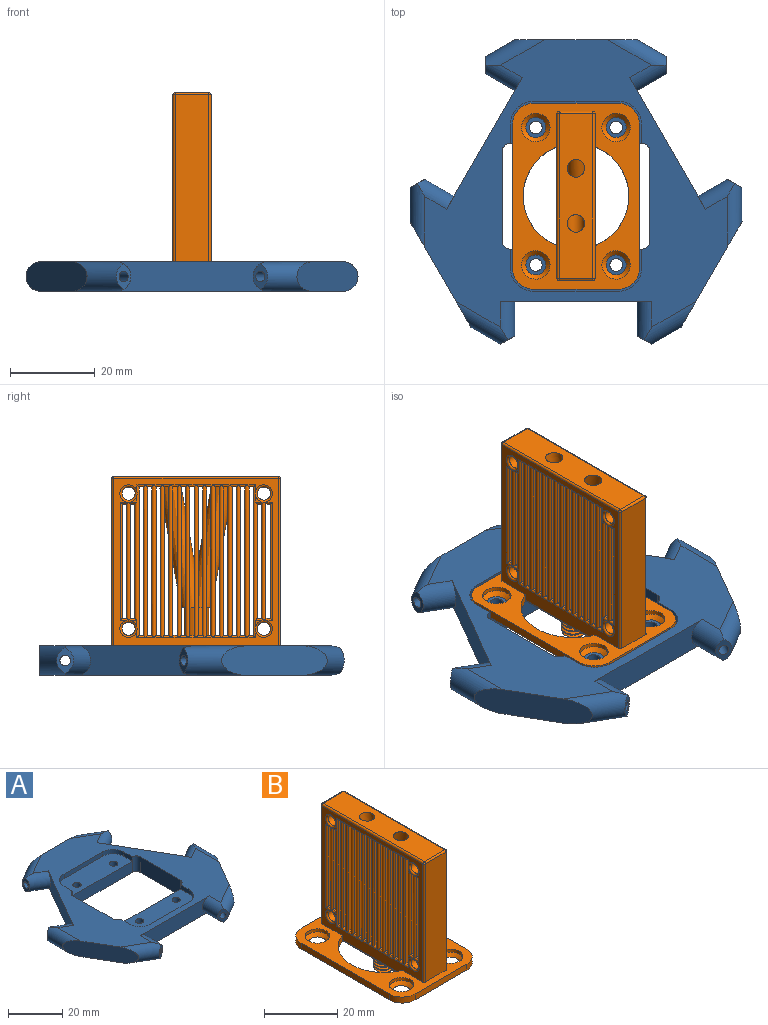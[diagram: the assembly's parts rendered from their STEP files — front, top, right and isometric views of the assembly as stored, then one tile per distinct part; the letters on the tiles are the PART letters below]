
ASSEMBLY  parts=2 mates=1
PART A: 53 faces, bbox 78.5x75.5x7 mm
  f0: plane 71.52x67.94mm, normal (0,0,1), area 1672.5mm2, adj f6,f8,f10,f12,f14,f16,f21,f22
  f1: cylinder r=1.5mm len=5mm, axis (0,0,1), area 47.1mm2, adj f5,f52
  f2: cylinder r=1.5mm len=5mm, axis (0,0,1), area 47.1mm2, adj f5,f52
  f3: cylinder r=1.5mm len=5mm, axis (0,0,1), area 47.1mm2, adj f5,f46
  f4: cylinder r=1.5mm len=5mm, axis (0,0,1), area 47.1mm2, adj f5,f46
  f5: plane 71.52x67.94mm, normal (0,0,-1), area 2238.2mm2, adj f1,f2,f3,f4,f6,f8,f10,f12
  f6: plane 31.06x17.93mm, normal (-0.87,0.5,0), area 212.6mm2, adj f0,f5,f21,f32
  f7: plane 6.04x3.46mm, normal (-0.5,0.87,0), area 12.2mm2, adj f20,f31,f32
  f8: plane 25x14.43mm, normal (-0.87,-0.5,0), area 181mm2, adj f0,f5,f30,f31
  f9: plane 6.04x3.46mm, normal (0.5,-0.87,0), area 12.2mm2, adj f20,f29,f30
  f10: plane 35.87x7mm, normal (0,-1,0), area 212.6mm2, adj f0,f5,f28,f29
  f11: plane 6.04x3.46mm, normal (-0.5,-0.87,0), area 12.2mm2, adj f19,f27,f28
  f12: plane 25x14.43mm, normal (0.87,-0.5,0), area 181mm2, adj f0,f5,f25,f27
  f13: plane 6.04x3.46mm, normal (0.5,0.87,0), area 12.2mm2, adj f19,f25,f26
  f14: plane 31.06x17.93mm, normal (0.87,0.5,0), area 212.6mm2, adj f0,f5,f24,f26
  f15: plane 6.04x4mm, normal (1,0,0), area 12.2mm2, adj f18,f23,f24
  f16: plane 28.87x7mm, normal (0,1,0), area 181mm2, adj f0,f5,f22,f23
  f17: plane 6.04x4mm, normal (-1,0,0), area 12.2mm2, adj f18,f21,f22
  f18: cylinder r=1.25mm len=42.72mm, axis (-1,0,0), area 335.6mm2, adj f15,f17
  f19: cylinder r=1.25mm len=38.25mm, axis (0.5,0.87,0), area 335.6mm2, adj f11,f13
  f20: cylinder r=1.25mm len=38.25mm, axis (0.5,-0.87,0), area 335.6mm2, adj f7,f9
  f21: cylinder r=3.5mm len=9.54mm, axis (-0.87,0.5,0), area 88.7mm2, adj f0,f5,f6,f17,f22
  f22: cylinder r=3.5mm len=14.79mm, axis (0.87,0.5,0), area 112.9mm2, adj f0,f5,f16,f17,f21
  f23: cylinder r=3.5mm len=14.79mm, axis (0.87,-0.5,0), area 112.9mm2, adj f0,f5,f15,f16,f24
  f24: cylinder r=3.5mm len=9.54mm, axis (-0.87,-0.5,0), area 88.7mm2, adj f0,f5,f14,f15,f23
  f25: cylinder r=3.5mm len=15.06mm, axis (0,-1,0), area 112.9mm2, adj f0,f5,f12,f13,f26
  f26: cylinder r=3.5mm len=9.54mm, axis (0.87,0.5,0), area 88.7mm2, adj f0,f5,f13,f14,f25
  f27: cylinder r=3.5mm len=14.79mm, axis (-0.87,-0.5,0), area 112.9mm2, adj f0,f5,f11,f12,f28
  f28: cylinder r=3.5mm len=9mm, axis (0,1,0), area 88.7mm2, adj f0,f5,f10,f11,f27
  f29: cylinder r=3.5mm len=9mm, axis (0,-1,0), area 88.7mm2, adj f0,f5,f9,f10,f30
  f30: cylinder r=3.5mm len=14.79mm, axis (-0.87,0.5,0), area 112.9mm2, adj f0,f5,f8,f9,f29
  f31: cylinder r=3.5mm len=15.06mm, axis (0,1,0), area 112.9mm2, adj f0,f5,f7,f8,f32
  f32: cylinder r=3.5mm len=9.54mm, axis (0.87,-0.5,0), area 88.7mm2, adj f0,f5,f6,f7,f31
  f33: plane 31x5mm, normal (0,1,0), area 155mm2, adj f5,f37,f39,f52
  f34: plane 21x7mm, normal (-1,0,0), area 147mm2, adj f0,f5,f39,f40
  f35: plane 31x5mm, normal (0,-1,0), area 155mm2, adj f5,f38,f40,f46
  f36: plane 21x7mm, normal (1,0,0), area 147mm2, adj f0,f5,f37,f38
  f37: cylinder r=2mm len=7mm, axis (0,0,-1), area 22mm2, adj f0,f5,f33,f36,f48
  f38: cylinder r=2mm len=7mm, axis (0,0,1), area 22mm2, adj f0,f5,f35,f36,f45
  f39: cylinder r=2mm len=7mm, axis (0,0,1), area 22mm2, adj f0,f5,f33,f34,f47
  f40: cylinder r=2mm len=7mm, axis (0,0,-1), area 22mm2, adj f0,f5,f34,f35,f41
  f41: plane 4.5x2mm, normal (-1,0,0), area 9mm2, adj f0,f40,f42,f46
  f42: cylinder r=5.5mm len=5.5mm, axis (0,0,1), area 17.3mm2, adj f0,f41,f43,f46
  f43: plane 20x2mm, normal (0,-1,0), area 40mm2, adj f0,f42,f44,f46
  f44: cylinder r=5.5mm len=5.5mm, axis (0,0,1), area 17.3mm2, adj f0,f43,f45,f46
  f45: plane 4.5x2mm, normal (1,0,0), area 9mm2, adj f0,f38,f44,f46
  f46: plane 31x10mm, normal (0,0,1), area 282.9mm2, adj f3,f4,f35,f41,f42,f43,f44,f45
  f47: plane 4.5x2mm, normal (-1,0,0), area 9mm2, adj f0,f39,f51,f52
  f48: plane 4.5x2mm, normal (1,0,0), area 9mm2, adj f0,f37,f49,f52
  f49: cylinder r=5.5mm len=5.5mm, axis (0,0,1), area 17.3mm2, adj f0,f48,f50,f52
  f50: plane 20x2mm, normal (0,1,0), area 40mm2, adj f0,f49,f51,f52
  f51: cylinder r=5.5mm len=5.5mm, axis (0,0,1), area 17.3mm2, adj f0,f47,f50,f52
  f52: plane 31x10mm, normal (0,0,1), area 282.9mm2, adj f1,f2,f33,f47,f48,f49,f50,f51
PART B: 283 faces, bbox 31x45x49.1 mm
  f0: plane 41x39mm, normal (1,0,0), area 285.2mm2, adj f65,f67,f68,f69,f70,f71,f72,f73
  f1: plane 41x39mm, normal (-1,0,0), area 285.2mm2, adj f6,f7,f9,f10,f11,f12,f13,f14
  f2: plane 4.93x4.85mm, normal (0,0,-1), area 11.5mm2, adj f258,f260,f261,f262,f263
  f3: cylinder r=2.95mm len=5.9mm, axis (0,0,-1), area 11.4mm2, adj f209,f261,f262,f263
  f4: cylinder r=1mm len=12.17mm, axis (0,-0.17,-0.98), area 64.1mm2, adj f5,f254,f259
  f5: cylinder r=1mm len=12.17mm, axis (0,0.17,-0.98), area 64.1mm2, adj f4,f256,f259
  f6: cylinder r=0.5mm len=2mm, axis (0,1,0), area 1.2mm2, adj f1,f8,f10,f160
  f7: cylinder r=0.5mm len=2mm, axis (0,-1,0), area 1.2mm2, adj f1,f8,f10,f206
  f8: cylinder r=0.5mm len=36.1mm, axis (0,0,-1), area 55.9mm2, adj f6,f7,f12,f13,f162,f205
  f9: torus R=2.05mm, axis (1,0,0), area 8.5mm2, adj f1,f10,f14,f16,f17,f145,f215
  f10: cylinder r=0.5mm len=36.1mm, axis (0,0,1), area 49.5mm2, adj f1,f6,f7,f9,f11,f17,f18,f174
  f11: torus R=2.05mm, axis (1,0,0), area 8.5mm2, adj f1,f10,f15,f16,f18,f148,f214
  f12: cylinder r=0.5mm len=2mm, axis (0,-1,0), area 1.2mm2, adj f1,f8,f20,f161
  f13: cylinder r=0.5mm len=2mm, axis (0,1,0), area 1.2mm2, adj f1,f8,f20,f163
  f14: cylinder r=0.5mm len=1.98mm, axis (0,1,0), area 1.2mm2, adj f1,f9,f16,f19,f150
  f15: cylinder r=0.5mm len=1.98mm, axis (0,-1,0), area 1.2mm2, adj f1,f11,f16,f19,f183
  f16: cylinder r=0.5mm len=27.95mm, axis (0,0,-1), area 43mm2, adj f9,f11,f14,f15,f17,f18,f143,f182
  f17: cylinder r=0.5mm len=1.98mm, axis (0,1,0), area 1.2mm2, adj f9,f10,f16,f173,f215
  f18: cylinder r=0.5mm len=1.98mm, axis (0,-1,0), area 1.2mm2, adj f10,f11,f16,f175,f214
  f19: cylinder r=0.5mm len=28mm, axis (0,0,-1), area 21.6mm2, adj f1,f14,f15,f184
  f20: cylinder r=0.5mm len=36.1mm, axis (0,0,-1), area 55.9mm2, adj f12,f13,f21,f22,f139,f165
  f21: cylinder r=0.5mm len=2mm, axis (0,-1,0), area 1.2mm2, adj f1,f20,f23,f164
  f22: cylinder r=0.5mm len=2mm, axis (0,1,0), area 1.2mm2, adj f1,f20,f23,f166
  f23: cylinder r=0.5mm len=36.1mm, axis (0,0,-1), area 55.9mm2, adj f21,f22,f24,f25,f140,f168
  f24: cylinder r=0.5mm len=2mm, axis (0,-1,0), area 1.2mm2, adj f1,f23,f26,f227
  f25: cylinder r=0.5mm len=2mm, axis (0,1,0), area 1.2mm2, adj f1,f23,f26,f169
  f26: cylinder r=0.5mm len=36.1mm, axis (0,0,-1), area 55.9mm2, adj f24,f25,f27,f28,f141,f171
  f27: cylinder r=0.5mm len=2mm, axis (0,-1,0), area 1.2mm2, adj f1,f26,f29,f228
  f28: cylinder r=0.5mm len=2mm, axis (0,1,0), area 1.2mm2, adj f1,f26,f29,f172
  f29: cylinder r=0.5mm len=36.1mm, axis (0,0,-1), area 55.9mm2, adj f27,f28,f30,f31,f142,f204
  f30: cylinder r=0.5mm len=2mm, axis (0,-1,0), area 1.2mm2, adj f1,f29,f32,f203
  f31: cylinder r=0.5mm len=2mm, axis (0,1,0), area 1.2mm2, adj f1,f29,f32,f159
  f32: cylinder r=0.5mm len=36.1mm, axis (0,0,-1), area 55.9mm2, adj f30,f31,f33,f34,f224,f226
  f33: cylinder r=0.5mm len=2mm, axis (0,-1,0), area 1.2mm2, adj f1,f32,f35,f202
  f34: cylinder r=0.5mm len=2mm, axis (0,1,0), area 1.2mm2, adj f1,f32,f35,f158
  f35: cylinder r=0.5mm len=36.1mm, axis (0,0,-1), area 55.9mm2, adj f33,f34,f36,f37,f218,f221
  f36: cylinder r=0.5mm len=2mm, axis (0,-1,0), area 1.2mm2, adj f1,f35,f38,f201
  f37: cylinder r=0.5mm len=2mm, axis (0,1,0), area 1.2mm2, adj f1,f35,f38,f219
  f38: cylinder r=0.5mm len=36.1mm, axis (0,0,-1), area 55.9mm2, adj f36,f37,f39,f40,f223,f225
  f39: cylinder r=0.5mm len=2mm, axis (0,-1,0), area 1.2mm2, adj f1,f38,f41,f200
  f40: cylinder r=0.5mm len=2mm, axis (0,1,0), area 1.2mm2, adj f1,f38,f41,f156
  f41: cylinder r=0.5mm len=36.1mm, axis (0,0,-1), area 55.9mm2, adj f39,f40,f42,f43,f199,f222
  f42: cylinder r=0.5mm len=2mm, axis (0,-1,0), area 1.2mm2, adj f1,f41,f44,f231
  f43: cylinder r=0.5mm len=2mm, axis (0,1,0), area 1.2mm2, adj f1,f41,f44,f155
  f44: cylinder r=0.5mm len=36.1mm, axis (0,0,-1), area 55.9mm2, adj f42,f43,f45,f46,f196,f197
  f45: cylinder r=0.5mm len=2mm, axis (0,-1,0), area 1.2mm2, adj f1,f44,f47,f230
  f46: cylinder r=0.5mm len=2mm, axis (0,1,0), area 1.2mm2, adj f1,f44,f47,f154
  f47: cylinder r=0.5mm len=36.1mm, axis (0,0,-1), area 55.9mm2, adj f45,f46,f48,f49,f193,f194
  f48: cylinder r=0.5mm len=2mm, axis (0,-1,0), area 1.2mm2, adj f1,f47,f50,f192
  f49: cylinder r=0.5mm len=2mm, axis (0,1,0), area 1.2mm2, adj f1,f47,f50,f153
  f50: cylinder r=0.5mm len=36.1mm, axis (0,0,-1), area 55.9mm2, adj f48,f49,f51,f52,f190,f191
  f51: cylinder r=0.5mm len=2mm, axis (0,-1,0), area 1.2mm2, adj f1,f50,f53,f189
  f52: cylinder r=0.5mm len=2mm, axis (0,1,0), area 1.2mm2, adj f1,f50,f53,f152
  f53: cylinder r=0.5mm len=36.1mm, axis (0,0,-1), area 55.9mm2, adj f51,f52,f54,f55,f187,f188
  f54: cylinder r=0.5mm len=2mm, axis (0,-1,0), area 1.2mm2, adj f1,f53,f57,f186
  f55: cylinder r=0.5mm len=2mm, axis (0,1,0), area 1.2mm2, adj f1,f53,f57,f151
  f56: torus R=2.05mm, axis (1,0,0), area 8.5mm2, adj f1,f57,f59,f61,f62,f147,f217
  f57: cylinder r=0.5mm len=36.1mm, axis (0,0,-1), area 49.5mm2, adj f1,f54,f55,f56,f58,f62,f63,f181
  f58: torus R=2.05mm, axis (1,0,0), area 8.5mm2, adj f1,f57,f60,f61,f63,f146,f216
  f59: cylinder r=0.5mm len=1.98mm, axis (0,-1,0), area 1.2mm2, adj f1,f56,f61,f64,f176
  f60: cylinder r=0.5mm len=1.98mm, axis (0,1,0), area 1.2mm2, adj f1,f58,f61,f64,f178
  f61: cylinder r=0.5mm len=27.95mm, axis (0,0,1), area 43mm2, adj f56,f58,f59,f60,f62,f63,f177,f179
  f62: cylinder r=0.5mm len=1.98mm, axis (0,-1,0), area 1.2mm2, adj f56,f57,f61,f180,f217
  f63: cylinder r=0.5mm len=1.98mm, axis (0,1,0), area 1.2mm2, adj f57,f58,f61,f149,f216
  f64: cylinder r=0.5mm len=28mm, axis (0,0,1), area 21.6mm2, adj f1,f59,f60,f144
  f65: cylinder r=0.5mm len=2mm, axis (0,-1,0), area 1.2mm2, adj f0,f66,f69,f160
  f66: cylinder r=0.5mm len=36.1mm, axis (0,0,1), area 55.9mm2, adj f65,f67,f71,f72,f162,f205
  f67: cylinder r=0.5mm len=2mm, axis (0,1,0), area 1.2mm2, adj f0,f66,f69,f206
  f68: torus R=2.05mm, axis (1,0,0), area 8.5mm2, adj f0,f69,f73,f75,f76,f148,f210
  f69: cylinder r=0.5mm len=36.1mm, axis (0,0,-1), area 49.5mm2, adj f0,f65,f67,f68,f70,f76,f77,f174
  f70: torus R=2.05mm, axis (1,0,0), area 8.5mm2, adj f0,f69,f74,f75,f77,f145,f211
  f71: cylinder r=0.5mm len=2mm, axis (0,-1,0), area 1.2mm2, adj f0,f66,f79,f163
  f72: cylinder r=0.5mm len=2mm, axis (0,1,0), area 1.2mm2, adj f0,f66,f79,f161
  f73: cylinder r=0.5mm len=1.98mm, axis (0,1,0), area 1.2mm2, adj f0,f68,f75,f78,f183
  f74: cylinder r=0.5mm len=1.98mm, axis (0,-1,0), area 1.2mm2, adj f0,f70,f75,f78,f150
  f75: cylinder r=0.5mm len=27.95mm, axis (0,0,1), area 43mm2, adj f68,f70,f73,f74,f76,f77,f143,f182
  f76: cylinder r=0.5mm len=1.98mm, axis (0,1,0), area 1.2mm2, adj f68,f69,f75,f175,f210
  f77: cylinder r=0.5mm len=1.98mm, axis (0,-1,0), area 1.2mm2, adj f69,f70,f75,f173,f211
  f78: cylinder r=0.5mm len=28mm, axis (0,0,1), area 21.6mm2, adj f0,f73,f74,f184
  f79: cylinder r=0.5mm len=36.1mm, axis (0,0,1), area 55.9mm2, adj f71,f72,f80,f81,f139,f165
  f80: cylinder r=0.5mm len=2mm, axis (0,-1,0), area 1.2mm2, adj f0,f79,f82,f166
  f81: cylinder r=0.5mm len=2mm, axis (0,1,0), area 1.2mm2, adj f0,f79,f82,f164
  f82: cylinder r=0.5mm len=36.1mm, axis (0,0,1), area 55.9mm2, adj f80,f81,f83,f84,f140,f168
  f83: cylinder r=0.5mm len=2mm, axis (0,-1,0), area 1.2mm2, adj f0,f82,f85,f169
  f84: cylinder r=0.5mm len=2mm, axis (0,1,0), area 1.2mm2, adj f0,f82,f85,f167
  f85: cylinder r=0.5mm len=36.1mm, axis (0,0,1), area 55.9mm2, adj f83,f84,f86,f87,f141,f171
  f86: cylinder r=0.5mm len=2mm, axis (0,-1,0), area 1.2mm2, adj f0,f85,f88,f172
  f87: cylinder r=0.5mm len=2mm, axis (0,1,0), area 1.2mm2, adj f0,f85,f88,f170
  f88: cylinder r=0.5mm len=36.1mm, axis (0,0,1), area 55.9mm2, adj f86,f87,f89,f90,f142,f204
  f89: cylinder r=0.5mm len=2mm, axis (0,-1,0), area 1.2mm2, adj f0,f88,f91,f159
  f90: cylinder r=0.5mm len=2mm, axis (0,1,0), area 1.2mm2, adj f0,f88,f91,f203
  f91: cylinder r=0.5mm len=36.1mm, axis (0,0,1), area 55.9mm2, adj f89,f90,f92,f93,f224,f226
  f92: cylinder r=0.5mm len=2mm, axis (0,-1,0), area 1.2mm2, adj f0,f91,f94,f220
  f93: cylinder r=0.5mm len=2mm, axis (0,1,0), area 1.2mm2, adj f0,f91,f94,f202
  f94: cylinder r=0.5mm len=36.1mm, axis (0,0,1), area 55.9mm2, adj f92,f93,f95,f96,f218,f221
  f95: cylinder r=0.5mm len=2mm, axis (0,-1,0), area 1.2mm2, adj f0,f94,f97,f157
  f96: cylinder r=0.5mm len=2mm, axis (0,1,0), area 1.2mm2, adj f0,f94,f97,f201
  f97: cylinder r=0.5mm len=36.1mm, axis (0,0,1), area 55.9mm2, adj f95,f96,f98,f99,f223,f225
  f98: cylinder r=0.5mm len=2mm, axis (0,-1,0), area 1.2mm2, adj f0,f97,f100,f156
  f99: cylinder r=0.5mm len=2mm, axis (0,1,0), area 1.2mm2, adj f0,f97,f100,f200
  f100: cylinder r=0.5mm len=36.1mm, axis (0,0,1), area 55.9mm2, adj f98,f99,f101,f102,f199,f222
  f101: cylinder r=0.5mm len=2mm, axis (0,-1,0), area 1.2mm2, adj f0,f100,f103,f155
  f102: cylinder r=0.5mm len=2mm, axis (0,1,0), area 1.2mm2, adj f0,f100,f103,f198
  f103: cylinder r=0.5mm len=36.1mm, axis (0,0,1), area 55.9mm2, adj f101,f102,f104,f105,f196,f197
  f104: cylinder r=0.5mm len=2mm, axis (0,-1,0), area 1.2mm2, adj f0,f103,f106,f154
  f105: cylinder r=0.5mm len=2mm, axis (0,1,0), area 1.2mm2, adj f0,f103,f106,f195
  f106: cylinder r=0.5mm len=36.1mm, axis (0,0,1), area 55.9mm2, adj f104,f105,f107,f108,f193,f194
  f107: cylinder r=0.5mm len=2mm, axis (0,-1,0), area 1.2mm2, adj f0,f106,f109,f153
  f108: cylinder r=0.5mm len=2mm, axis (0,1,0), area 1.2mm2, adj f0,f106,f109,f192
  f109: cylinder r=0.5mm len=36.1mm, axis (0,0,1), area 55.9mm2, adj f107,f108,f110,f111,f190,f191
  f110: cylinder r=0.5mm len=2mm, axis (0,-1,0), area 1.2mm2, adj f0,f109,f112,f152
  f111: cylinder r=0.5mm len=2mm, axis (0,1,0), area 1.2mm2, adj f0,f109,f112,f189
  f112: cylinder r=0.5mm len=36.1mm, axis (0,0,1), area 55.9mm2, adj f110,f111,f113,f114,f187,f188
  f113: cylinder r=0.5mm len=2mm, axis (0,-1,0), area 1.2mm2, adj f0,f112,f116,f151
  f114: cylinder r=0.5mm len=2mm, axis (0,1,0), area 1.2mm2, adj f0,f112,f116,f186
  f115: torus R=2.05mm, axis (1,0,0), area 8.5mm2, adj f0,f116,f118,f120,f121,f146,f212
  f116: cylinder r=0.5mm len=36.1mm, axis (0,0,1), area 49.5mm2, adj f0,f113,f114,f115,f117,f121,f122,f181
  f117: torus R=2.05mm, axis (1,0,0), area 8.5mm2, adj f0,f116,f119,f120,f122,f147,f213
  f118: cylinder r=0.5mm len=1.98mm, axis (0,-1,0), area 1.2mm2, adj f0,f115,f120,f123,f178
  f119: cylinder r=0.5mm len=1.98mm, axis (0,1,0), area 1.2mm2, adj f0,f117,f120,f123,f176
  f120: cylinder r=0.5mm len=27.95mm, axis (0,0,-1), area 43mm2, adj f115,f117,f118,f119,f121,f122,f177,f179
  f121: cylinder r=0.5mm len=1.98mm, axis (0,-1,0), area 1.2mm2, adj f115,f116,f120,f149,f212
  f122: cylinder r=0.5mm len=1.98mm, axis (0,1,0), area 1.2mm2, adj f116,f117,f120,f180,f213
  f123: cylinder r=0.5mm len=28mm, axis (0,0,-1), area 21.6mm2, adj f0,f118,f119,f144
  f124: cylinder r=0.5mm len=39.5mm, axis (0,0,1), area 31mm2, adj f0,f128,f208,f278
  f125: cylinder r=0.5mm len=23.69mm, axis (0,1,0), area 18.5mm2, adj f0,f209,f264
  f126: cylinder r=0.5mm len=23.68mm, axis (0,-1,0), area 18.5mm2, adj f1,f209,f268
  f127: cylinder r=0.5mm len=39.5mm, axis (0,0,-1), area 31mm2, adj f1,f129,f208,f278
  f128: sphere r=0.5mm, area 0.2mm2, adj f124,f130,f131
  f129: sphere r=0.5mm, area 0.5mm2, adj f127,f130,f134
  f130: cylinder r=0.5mm len=8mm, axis (1,0,0), area 6.3mm2, adj f128,f129,f208,f229
  f131: cylinder r=0.5mm len=39mm, axis (0,-1,0), area 30.6mm2, adj f0,f128,f135,f229
  f132: cylinder r=0.5mm len=39.5mm, axis (0,0,-1), area 31mm2, adj f0,f135,f138,f278
  f133: cylinder r=0.5mm len=39.5mm, axis (0,0,1), area 31mm2, adj f1,f136,f138,f278
  f134: cylinder r=0.5mm len=39mm, axis (0,1,0), area 30.6mm2, adj f1,f129,f136,f229
  f135: sphere r=0.5mm, area 0.2mm2, adj f131,f132,f137
  f136: sphere r=0.5mm, area 0.3mm2, adj f133,f134,f137
  f137: cylinder r=0.5mm len=8mm, axis (-1,0,0), area 6.3mm2, adj f135,f136,f138,f229
  f138: plane 39.5x8mm, normal (0,-1,0), area 316mm2, adj f132,f133,f137,f278
  f139: plane 35.1x8mm, normal (0,-1,0), area 280.8mm2, adj f20,f79,f161,f163
  f140: plane 35.1x8mm, normal (0,-1,0), area 280mm2, adj f23,f82,f164,f166,f245
  f141: plane 35.1x8mm, normal (0,-1,0), area 235.8mm2, adj f26,f85,f167,f169,f227,f246
  f142: plane 35.1x8mm, normal (0,-1,0), area 182.3mm2, adj f29,f88,f170,f172,f228,f247
  f143: plane 27x8mm, normal (0,1,0), area 216mm2, adj f16,f75,f173,f175
  f144: plane 27x8mm, normal (0,-1,0), area 216mm2, adj f64,f123,f176,f178
  f145: cylinder r=1.55mm len=8mm, axis (1,0,0), area 77.9mm2, adj f9,f70
  f146: cylinder r=1.55mm len=8mm, axis (1,0,0), area 77.9mm2, adj f58,f115
  f147: cylinder r=1.55mm len=8mm, axis (1,0,0), area 77.9mm2, adj f56,f117
  f148: cylinder r=1.55mm len=8mm, axis (1,0,0), area 77.9mm2, adj f11,f68
  f149: plane 8x1mm, normal (0,0,1), area 8mm2, adj f63,f121,f179,f181
  f150: plane 8x1mm, normal (0,0,1), area 8mm2, adj f14,f74,f182,f184
  f151: plane 8x1mm, normal (0,0,1), area 8mm2, adj f55,f113,f185,f187
  f152: plane 8x1mm, normal (0,0,1), area 8mm2, adj f52,f110,f188,f190
  f153: plane 8x1mm, normal (0,0,1), area 8mm2, adj f49,f107,f191,f193
  f154: plane 8x1mm, normal (0,0,1), area 8mm2, adj f46,f104,f194,f196
  f155: plane 8x1mm, normal (0,0,1), area 8mm2, adj f43,f101,f197,f199
  f156: plane 8x1mm, normal (0,0,1), area 7mm2, adj f40,f98,f222,f223,f252
  f157: plane 1.46x1mm, normal (0,0,1), area 1.2mm2, adj f95,f218,f225,f238
  f158: plane 1.46x1mm, normal (0,0,1), area 1.2mm2, adj f34,f221,f226,f243
  f159: plane 8x1mm, normal (0,0,1), area 7mm2, adj f31,f89,f204,f224,f233
  f160: plane 8x1mm, normal (0,0,1), area 8mm2, adj f6,f65,f205,f207
  f161: plane 8x1mm, normal (0,0,-1), area 8mm2, adj f12,f72,f139,f162
  f162: plane 35.1x8mm, normal (0,1,0), area 280.8mm2, adj f8,f66,f161,f163
  f163: plane 8x1mm, normal (0,0,1), area 8mm2, adj f13,f71,f139,f162
  f164: plane 8.05x1.05mm, normal (0,0,-1), area 7.9mm2, adj f21,f81,f140,f165,f245
  f165: plane 35.1x8mm, normal (0,1,0), area 280.8mm2, adj f20,f79,f164,f166
  f166: plane 8x1mm, normal (0,0,1), area 8mm2, adj f22,f80,f140,f165
  f167: plane 1.93x1.01mm, normal (0,0,-1), area 1.7mm2, adj f84,f141,f168,f246
  f168: plane 35.1x8mm, normal (0,1,0), area 262mm2, adj f23,f82,f167,f169,f227,f246
  f169: plane 8x1mm, normal (0,0,1), area 8mm2, adj f25,f83,f141,f168
  f170: plane 2.06x1.01mm, normal (0,0,-1), area 1.8mm2, adj f87,f142,f171,f247
  f171: plane 35.1x8mm, normal (0,1,0), area 207.6mm2, adj f26,f85,f170,f172,f228,f247
  f172: plane 8x1mm, normal (0,0,1), area 8mm2, adj f28,f86,f142,f171
  f173: plane 8x1mm, normal (0,0,1), area 8mm2, adj f17,f77,f143,f174
  f174: plane 27x8mm, normal (0,-1,0), area 216mm2, adj f10,f69,f173,f175
  f175: plane 8x1mm, normal (0,0,-1), area 8mm2, adj f18,f76,f143,f174
  f176: plane 8x1mm, normal (0,0,-1), area 8mm2, adj f59,f119,f144,f177
  f177: plane 27x8mm, normal (0,1,0), area 216mm2, adj f61,f120,f176,f178
  f178: plane 8x1mm, normal (0,0,1), area 8mm2, adj f60,f118,f144,f177
  f179: plane 27x8mm, normal (0,-1,0), area 216mm2, adj f61,f120,f149,f180
  f180: plane 8x1mm, normal (0,0,-1), area 8mm2, adj f62,f122,f179,f181
  f181: plane 27x8mm, normal (0,1,0), area 216mm2, adj f57,f116,f149,f180
  f182: plane 27x8mm, normal (0,-1,0), area 216mm2, adj f16,f75,f150,f183
  f183: plane 8x1mm, normal (0,0,-1), area 8mm2, adj f15,f73,f182,f184
  f184: plane 27x8mm, normal (0,1,0), area 216mm2, adj f19,f78,f150,f183
  f185: plane 35.1x8mm, normal (0,-1,0), area 280.8mm2, adj f57,f116,f151,f186
  f186: plane 8x1mm, normal (0,0,-1), area 8mm2, adj f54,f114,f185,f187
  f187: plane 35.1x8mm, normal (0,1,0), area 280.8mm2, adj f53,f112,f151,f186
  f188: plane 35.1x8mm, normal (0,-1,0), area 280.8mm2, adj f53,f112,f152,f189
  f189: plane 8x1mm, normal (0,0,-1), area 8mm2, adj f51,f111,f188,f190
  f190: plane 35.1x8mm, normal (0,1,0), area 280.8mm2, adj f50,f109,f152,f189
  f191: plane 35.1x8mm, normal (0,-1,0), area 280.8mm2, adj f50,f109,f153,f192
  f192: plane 8.05x1.05mm, normal (0,0,-1), area 7.9mm2, adj f48,f108,f191,f193,f248
  f193: plane 35.1x8mm, normal (0,1,0), area 280mm2, adj f47,f106,f153,f192,f248
  f194: plane 35.1x8mm, normal (0,-1,0), area 262mm2, adj f47,f106,f154,f195,f230,f249
  f195: plane 1.93x1.01mm, normal (0,0,-1), area 1.7mm2, adj f105,f194,f196,f249
  f196: plane 35.1x8mm, normal (0,1,0), area 235.8mm2, adj f44,f103,f154,f195,f230,f249
  f197: plane 35.1x8mm, normal (0,-1,0), area 207.6mm2, adj f44,f103,f155,f198,f231,f250
  f198: plane 2.06x1.01mm, normal (0,0,-1), area 1.8mm2, adj f102,f197,f199,f250
  f199: plane 35.1x8mm, normal (0,1,0), area 182.3mm2, adj f41,f100,f155,f198,f231,f250
  f200: plane 8x1mm, normal (0,0,-1), area 8mm2, adj f39,f99,f222,f223
  f201: plane 8x1mm, normal (0,0,-1), area 8mm2, adj f36,f96,f218,f225
  f202: plane 8x1mm, normal (0,0,-1), area 8mm2, adj f33,f93,f221,f226
  f203: plane 8x1mm, normal (0,0,-1), area 8mm2, adj f30,f90,f204,f224
  f204: plane 35.1x8mm, normal (0,1,0), area 168.2mm2, adj f29,f88,f159,f203,f232,f234
  f205: plane 35.1x8mm, normal (0,-1,0), area 280.8mm2, adj f8,f66,f160,f206
  f206: plane 8x1mm, normal (0,0,-1), area 8mm2, adj f7,f67,f205,f207
  f207: plane 35.1x8mm, normal (0,1,0), area 280.8mm2, adj f10,f69,f160,f206
  f208: plane 39.5x8mm, normal (0,1,0), area 316mm2, adj f124,f127,f130,f278
  f209: plane 44.28x30.28mm, normal (0,0,-1), area 912.2mm2, adj f3,f125,f126,f260,f261,f262,f264,f265
  f210: plane 1.55x1.55mm, normal (1,0,0), area 0.7mm2, adj f68,f69,f76
  f211: plane 1.55x1.55mm, normal (1,0,0), area 0.7mm2, adj f69,f70,f77
  f212: plane 1.55x1.55mm, normal (1,0,0), area 0.7mm2, adj f115,f116,f121
  f213: plane 1.55x1.55mm, normal (1,0,0), area 0.7mm2, adj f116,f117,f122
  f214: plane 1.55x1.55mm, normal (-1,0,0), area 0.7mm2, adj f10,f11,f18
  f215: plane 1.55x1.55mm, normal (-1,0,0), area 0.7mm2, adj f9,f10,f17
  f216: plane 1.55x1.55mm, normal (-1,0,0), area 0.7mm2, adj f57,f58,f63
  f217: plane 1.55x1.55mm, normal (-1,0,0), area 0.7mm2, adj f56,f57,f62
  f218: plane 35.1x8mm, normal (0,1,0), area 201.9mm2, adj f35,f94,f157,f201,f219,f235,f236,f237
  f219: plane 1.46x1mm, normal (0,0,1), area 1.2mm2, adj f37,f218,f225,f236
  f220: plane 1.46x1mm, normal (0,0,1), area 1.2mm2, adj f92,f221,f226,f241
  f221: plane 35.1x8mm, normal (0,-1,0), area 201.9mm2, adj f35,f94,f158,f202,f220,f240,f241,f242
  f222: plane 35.1x8mm, normal (0,-1,0), area 168.2mm2, adj f41,f100,f156,f200,f251,f253
  f223: plane 35.1x8mm, normal (0,1,0), area 165.2mm2, adj f38,f97,f156,f200,f251,f252,f253
  f224: plane 35.1x8mm, normal (0,-1,0), area 165.2mm2, adj f32,f91,f159,f203,f232,f233,f234
  f225: plane 35.1x8mm, normal (0,-1,0), area 178.5mm2, adj f38,f97,f157,f201,f219,f235,f236,f237
  f226: plane 35.1x8mm, normal (0,1,0), area 178.5mm2, adj f32,f91,f158,f202,f220,f240,f241,f242
  f227: plane 1.93x1.01mm, normal (0,0,-1), area 1.7mm2, adj f24,f141,f168,f246
  f228: plane 2.06x1.01mm, normal (0,0,-1), area 1.8mm2, adj f27,f142,f171,f247
  f229: plane 39.98x8.98mm, normal (0,0,1), area 285.2mm2, adj f130,f131,f134,f137,f255,f257
  f230: plane 1.93x1.01mm, normal (0,0,-1), area 1.7mm2, adj f45,f194,f196,f249
  f231: plane 2.06x1.01mm, normal (0,0,-1), area 1.8mm2, adj f42,f197,f199,f250
  f232: plane 4.16x1.04mm, normal (0,0,-1), area 2.1mm2, adj f204,f224,f233,f234
  f233: cylinder r=2.95mm len=6.55mm, axis (0,0,-1), area 21.6mm2, adj f159,f224,f232
  f234: cylinder r=2.5mm len=28.58mm, axis (0,0.17,-0.98), area 71mm2, adj f204,f224,f232
  f235: plane 1x0.47mm, normal (0,0,1), area 0.3mm2, adj f218,f225,f236,f239
  f236: cylinder r=2.95mm len=6.55mm, axis (0,0,-1), area 7mm2, adj f218,f219,f225,f235
  f237: plane 1x0.47mm, normal (0,0,1), area 0.3mm2, adj f218,f225,f238,f239
  f238: cylinder r=2.95mm len=6.55mm, axis (0,0,-1), area 7mm2, adj f157,f218,f225,f237
  f239: cylinder r=2.5mm len=17.13mm, axis (0,-0.17,-0.98), area 44.6mm2, adj f218,f225,f235,f237
  f240: plane 1x0.47mm, normal (0,0,1), area 0.3mm2, adj f221,f226,f241,f244
  f241: cylinder r=2.95mm len=6.55mm, axis (0,0,-1), area 7mm2, adj f220,f221,f226,f240
  f242: plane 1x0.47mm, normal (0,0,1), area 0.3mm2, adj f221,f226,f243,f244
  f243: cylinder r=2.95mm len=6.55mm, axis (0,0,-1), area 7mm2, adj f158,f221,f226,f242
  f244: cylinder r=2.5mm len=17.13mm, axis (0,0.17,-0.98), area 44.6mm2, adj f221,f226,f240,f242
  f245: cylinder r=2.5mm len=1.58mm, axis (0,0.17,-0.98), area 0.8mm2, adj f140,f164
  f246: cylinder r=2.5mm len=12.29mm, axis (0,0.17,-0.98), area 34.6mm2, adj f141,f167,f168,f227
  f247: cylinder r=2.5mm len=23.69mm, axis (0,0.17,-0.98), area 58.2mm2, adj f142,f170,f171,f228
  f248: cylinder r=2.5mm len=1.58mm, axis (0,-0.17,-0.98), area 0.8mm2, adj f192,f193
  f249: cylinder r=2.5mm len=12.29mm, axis (0,-0.17,-0.98), area 34.6mm2, adj f194,f195,f196,f230
  f250: cylinder r=2.5mm len=23.69mm, axis (0,-0.17,-0.98), area 58.2mm2, adj f197,f198,f199,f231
  f251: plane 4.16x1.04mm, normal (0,0,-1), area 2.1mm2, adj f222,f223,f252,f253
  f252: cylinder r=2.95mm len=6.55mm, axis (0,0,-1), area 21.6mm2, adj f156,f223,f251
  f253: cylinder r=2.5mm len=28.58mm, axis (0,-0.17,-0.98), area 71mm2, adj f222,f223,f251
  f254: plane 4.1x4.04mm, normal (0,0.17,0.98), area 10.1mm2, adj f4,f255
  f255: cylinder r=2.05mm len=26.25mm, axis (0,0.17,0.98), area 331.7mm2, adj f229,f254
  f256: plane 4.1x4.04mm, normal (0,-0.17,0.98), area 10.1mm2, adj f5,f257
  f257: cylinder r=2.05mm len=26.25mm, axis (0,-0.17,0.98), area 329.4mm2, adj f229,f256
  f258: cylinder r=1.5mm len=10mm, axis (0,0,-1), area 94.2mm2, adj f2,f259
  f259: plane 3.35x3.35mm, normal (0,0,-1), area 3.9mm2, adj f4,f5,f258
  f260: bspline ~5.75x5.56mm, area 20.9mm2, adj f2,f209,f261,f262
  f261: bspline ~6.81x5.9mm, area 51.4mm2, adj f2,f3,f209,f260,f263
  f262: bspline ~6.81x5.9mm, area 51.4mm2, adj f2,f3,f209,f260,f263
  f263: cone r=2.95mm half-angle=63.4deg, axis (0,0,1), area 3.8mm2, adj f2,f3,f261,f262
  f264: cylinder r=12.5mm len=23.69mm, axis (0,0,-1), area 60.4mm2, adj f0,f125,f209,f278
  f265: plane 20x2mm, normal (0,1,0), area 40mm2, adj f209,f278,f279,f282
  f266: plane 34x2mm, normal (-1,0,0), area 68mm2, adj f209,f278,f281,f282
  f267: plane 20x2mm, normal (0,-1,0), area 40mm2, adj f209,f278,f280,f281
  f268: cylinder r=12.5mm len=23.68mm, axis (0,0,-1), area 60.4mm2, adj f1,f126,f209,f278
  f269: plane 34x2mm, normal (1,0,0), area 68mm2, adj f209,f278,f279,f280
  f270: cone r=1.7mm half-angle=45deg, axis (0,0,1), area 25.4mm2, adj f209,f274
  f271: cone r=1.7mm half-angle=45deg, axis (0,0,1), area 25.4mm2, adj f209,f275
  f272: cone r=1.7mm half-angle=45deg, axis (0,0,1), area 25.4mm2, adj f209,f276
  f273: cone r=1.7mm half-angle=45deg, axis (0,0,1), area 25.4mm2, adj f209,f277
  f274: cylinder r=3.36mm len=6.72mm, axis (0,0,-1), area 21.1mm2, adj f270,f278
  f275: cylinder r=3.36mm len=6.72mm, axis (0,0,-1), area 21.1mm2, adj f271,f278
  f276: cylinder r=3.36mm len=6.72mm, axis (0,0,-1), area 21.1mm2, adj f272,f278
  f277: cylinder r=3.36mm len=6.72mm, axis (0,0,-1), area 21.1mm2, adj f273,f278
  f278: plane 44x30mm, normal (0,0,1), area 526.1mm2, adj f0,f1,f124,f127,f132,f133,f138,f208
  f279: cylinder r=5mm len=5mm, axis (0,0,-1), area 15.7mm2, adj f209,f265,f269,f278
  f280: cylinder r=5mm len=5mm, axis (0,0,1), area 15.7mm2, adj f209,f267,f269,f278
  f281: cylinder r=5mm len=5mm, axis (0,0,-1), area 15.7mm2, adj f209,f266,f267,f278
  f282: cylinder r=5mm len=5mm, axis (0,0,1), area 15.7mm2, adj f209,f265,f266,f278
PLACE A t=(10.3,11.74,31.14)mm
PLACE B t=(-4.7,3.75,21.14)mm
MATE fastened B.f273 <-> A.f1  axis (0,0,-1) through (0.8,-4.51,36.14)mm
